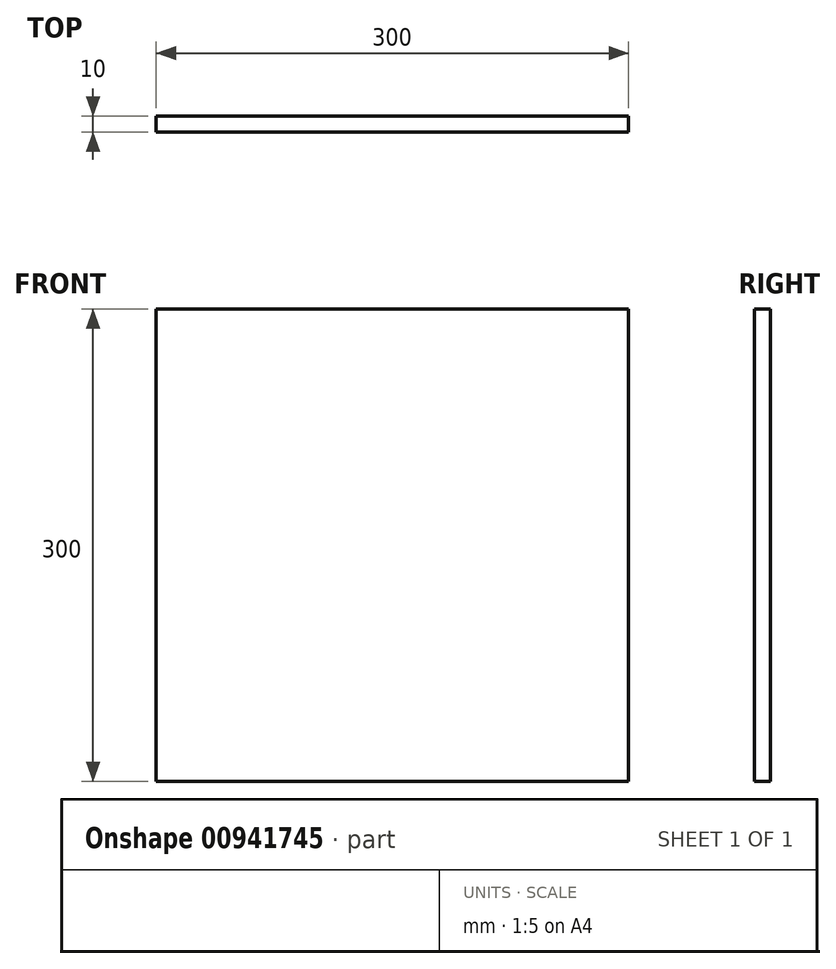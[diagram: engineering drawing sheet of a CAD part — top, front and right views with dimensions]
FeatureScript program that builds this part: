
annotation { "Feature Type Name" : "Feature", "Feature Type Description" : "" }
export const myFeature = defineFeature(function(context is Context, id is Id, definition is map)
    precondition{}
    {
        {
            var Q0;
            Q0=qCreatedBy(makeId("Right.planeOp"),FACE);
            var sketch = newSketch(context, id + "F0", { "sketchPlane" : qUnion([Q0])});
            skLineSegment(sketch, "E0.bottom", {"start": v(0, 0) * mm, "end": v(10, 0) * mm});
            skLineSegment(sketch, "E0.top", {"start": v(0, 300) * mm, "end": v(10, 300) * mm});
            skLineSegment(sketch, "E0.left", {"start": v(0, 0) * mm, "end": v(0, 300) * mm});
            skLineSegment(sketch, "E0.right", {"start": v(10, 0) * mm, "end": v(10, 300) * mm});
            skLineSegment(sketch, "E1.bottom", {"start": v(10, 300) * mm, "end": v(0, 300) * mm});
            skLineSegment(sketch, "E1.top", {"start": v(10, 450) * mm, "end": v(0, 450) * mm});
            skLineSegment(sketch, "E1.left", {"start": v(10, 300) * mm, "end": v(10, 450) * mm});
            skLineSegment(sketch, "E1.right", {"start": v(0, 300) * mm, "end": v(0, 450) * mm});
            skSolve(sketch);
        }
        {
            var Q0;
            Q0=makeQuery(id+"F0.imprint","IMPRINT",FACE,{"disambiguationData":[TD([[makeQuery(id+"F0.imprint","IMPRINT",EDGE,{"derivedFrom":sQuery(id+"F0.wireOp",EDGE,"E0.bottom")}),1.0]])]});
            extrude(context, id + "F1", {"entities" : qUnion([Q0]), "depth" : 300 * mm, "offsetDistance" : 25 * mm});
        }
    });
